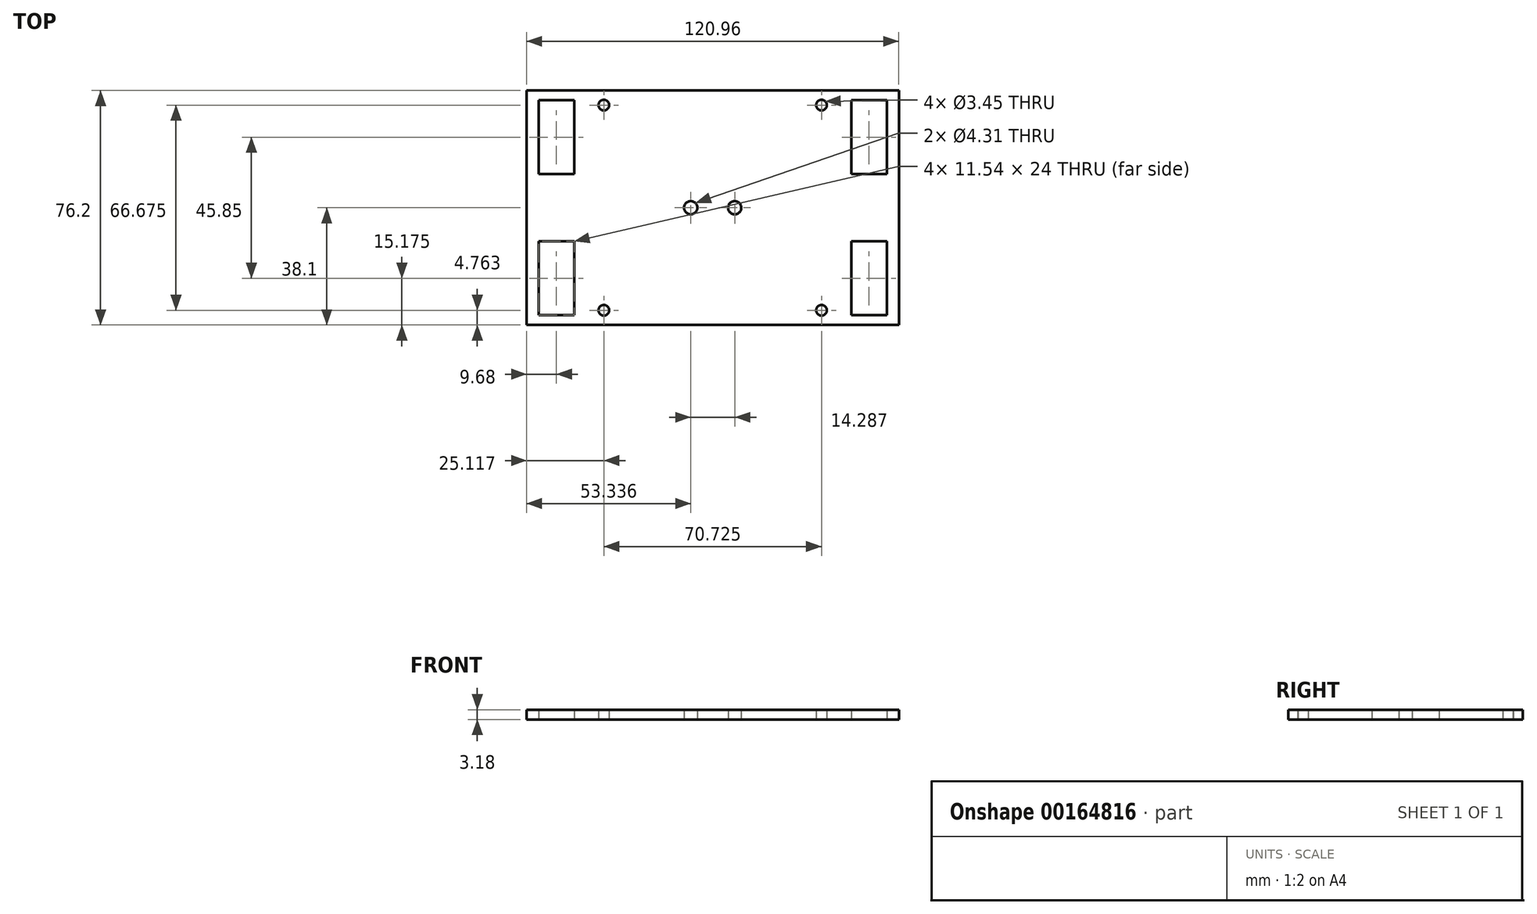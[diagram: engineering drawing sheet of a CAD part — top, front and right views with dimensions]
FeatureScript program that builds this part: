
annotation { "Feature Type Name" : "Feature", "Feature Type Description" : "" }
export const myFeature = defineFeature(function(context is Context, id is Id, definition is map)
    precondition{}
    {
        {
            var Q0;
            Q0=qCreatedBy(makeId("Top.planeOp"),FACE);
            var sketch = newSketch(context, id + "F0", { "sketchPlane" : qUnion([Q0])});
            skLineSegment(sketch, "E0.bottom", {"start": v(60.48, -38.1) * mm, "end": v(-60.48, -38.1) * mm});
            skLineSegment(sketch, "E0.top", {"start": v(60.48, 38.1) * mm, "end": v(-60.48, 38.1) * mm});
            skLineSegment(sketch, "E0.left", {"start": v(60.48, -38.1) * mm, "end": v(60.48, 38.1) * mm});
            skLineSegment(sketch, "E0.right", {"start": v(-60.48, -38.1) * mm, "end": v(-60.48, 38.1) * mm});
            skPoint(sketch, "E0.middle", {"position": v(0, 0) * mm});
            skLineSegment(sketch, "E1.bottom", {"start": v(50.8, -22.93) * mm, "end": v(-50.8, -22.93) * mm, "construction": true});
            skLineSegment(sketch, "E1.top", {"start": v(50.8, 22.93) * mm, "end": v(-50.8, 22.93) * mm, "construction": true});
            skLineSegment(sketch, "E1.left", {"start": v(50.8, -22.93) * mm, "end": v(50.8, 22.93) * mm, "construction": true});
            skLineSegment(sketch, "E1.right", {"start": v(-50.8, -22.93) * mm, "end": v(-50.8, 22.93) * mm, "construction": true});
            skLineSegment(sketch, "E2.bottom", {"start": v(45.03, -10.93) * mm, "end": v(56.57, -10.93) * mm});
            skLineSegment(sketch, "E2.top", {"start": v(45.03, -34.93) * mm, "end": v(56.57, -34.93) * mm});
            skLineSegment(sketch, "E2.left", {"start": v(45.03, -10.93) * mm, "end": v(45.03, -34.93) * mm});
            skLineSegment(sketch, "E2.right", {"start": v(56.57, -10.93) * mm, "end": v(56.57, -34.93) * mm});
            skPoint(sketch, "E2.middle", {"position": v(50.8, -22.93) * mm});
            skLineSegment(sketch, "E3.bottom", {"start": v(56.57, 34.93) * mm, "end": v(45.03, 34.93) * mm});
            skLineSegment(sketch, "E3.top", {"start": v(56.57, 10.93) * mm, "end": v(45.03, 10.93) * mm});
            skLineSegment(sketch, "E3.left", {"start": v(56.57, 34.93) * mm, "end": v(56.57, 10.93) * mm});
            skLineSegment(sketch, "E3.right", {"start": v(45.03, 34.93) * mm, "end": v(45.03, 10.93) * mm});
            skPoint(sketch, "E3.middle", {"position": v(50.8, 22.93) * mm});
            skLineSegment(sketch, "E4.bottom", {"start": v(-45.03, 34.93) * mm, "end": v(-56.57, 34.93) * mm});
            skLineSegment(sketch, "E4.top", {"start": v(-45.03, 10.93) * mm, "end": v(-56.57, 10.93) * mm});
            skLineSegment(sketch, "E4.left", {"start": v(-45.03, 34.93) * mm, "end": v(-45.03, 10.93) * mm});
            skLineSegment(sketch, "E4.right", {"start": v(-56.57, 34.93) * mm, "end": v(-56.57, 10.93) * mm});
            skPoint(sketch, "E4.middle", {"position": v(-50.8, 22.93) * mm});
            skLineSegment(sketch, "E5.bottom", {"start": v(-45.03, -10.93) * mm, "end": v(-56.57, -10.93) * mm});
            skLineSegment(sketch, "E5.top", {"start": v(-45.03, -34.93) * mm, "end": v(-56.57, -34.93) * mm});
            skLineSegment(sketch, "E5.left", {"start": v(-45.03, -10.93) * mm, "end": v(-45.03, -34.93) * mm});
            skLineSegment(sketch, "E5.right", {"start": v(-56.57, -10.93) * mm, "end": v(-56.57, -34.93) * mm});
            skPoint(sketch, "E5.middle", {"position": v(-50.8, -22.93) * mm});
            skLineSegment(sketch, "E6", {"start": v(56.57, -34.93) * mm, "end": v(56.57, -38.1) * mm, "construction": true});
            skLineSegment(sketch, "E7", {"start": v(56.57, -34.93) * mm, "end": v(60.48, -34.93) * mm, "construction": true});
            skLineSegment(sketch, "E8.bottom", {"start": v(35.36, -33.34) * mm, "end": v(-35.36, -33.34) * mm, "construction": true});
            skLineSegment(sketch, "E8.top", {"start": v(35.36, 33.34) * mm, "end": v(-35.36, 33.34) * mm, "construction": true});
            skLineSegment(sketch, "E8.left", {"start": v(35.36, -33.34) * mm, "end": v(35.36, 33.34) * mm, "construction": true});
            skLineSegment(sketch, "E8.right", {"start": v(-35.36, -33.34) * mm, "end": v(-35.36, 33.34) * mm, "construction": true});
            skLineSegment(sketch, "E9", {"start": v(35.36, -33.34) * mm, "end": v(35.36, -38.1) * mm, "construction": true});
            skLineSegment(sketch, "E10", {"start": v(35.36, -33.34) * mm, "end": v(50.8, -33.34) * mm, "construction": true});
            skLineSegment(sketch, "E11", {"start": v(50.8, -33.34) * mm, "end": v(50.8, -22.93) * mm, "construction": true});
            skCircle(sketch, "E12", {"center": v(-35.36, 33.34) * mm, "radius": 1.73 * mm});
            skCircle(sketch, "E13", {"center": v(35.36, -33.34) * mm, "radius": 1.73 * mm});
            skCircle(sketch, "E14", {"center": v(-35.36, -33.34) * mm, "radius": 1.73 * mm});
            skCircle(sketch, "E15", {"center": v(35.36, 33.34) * mm, "radius": 1.73 * mm});
            skLineSegment(sketch, "E16", {"start": v(-7.14, 0) * mm, "end": v(7.14, 0) * mm, "construction": true});
            skCircle(sketch, "E17", {"center": v(-7.14, 0) * mm, "radius": 2.15 * mm});
            skCircle(sketch, "E18", {"center": v(7.14, 0) * mm, "radius": 2.15 * mm});
            skSolve(sketch);
        }
        {
            var Q0;
            Q0 = qSketchRegion(id + "F0", true);
            extrude(context, id + "F1", {"entities" : qUnion([Q0]), "depth" : 3.17 * mm});
        }
    });
